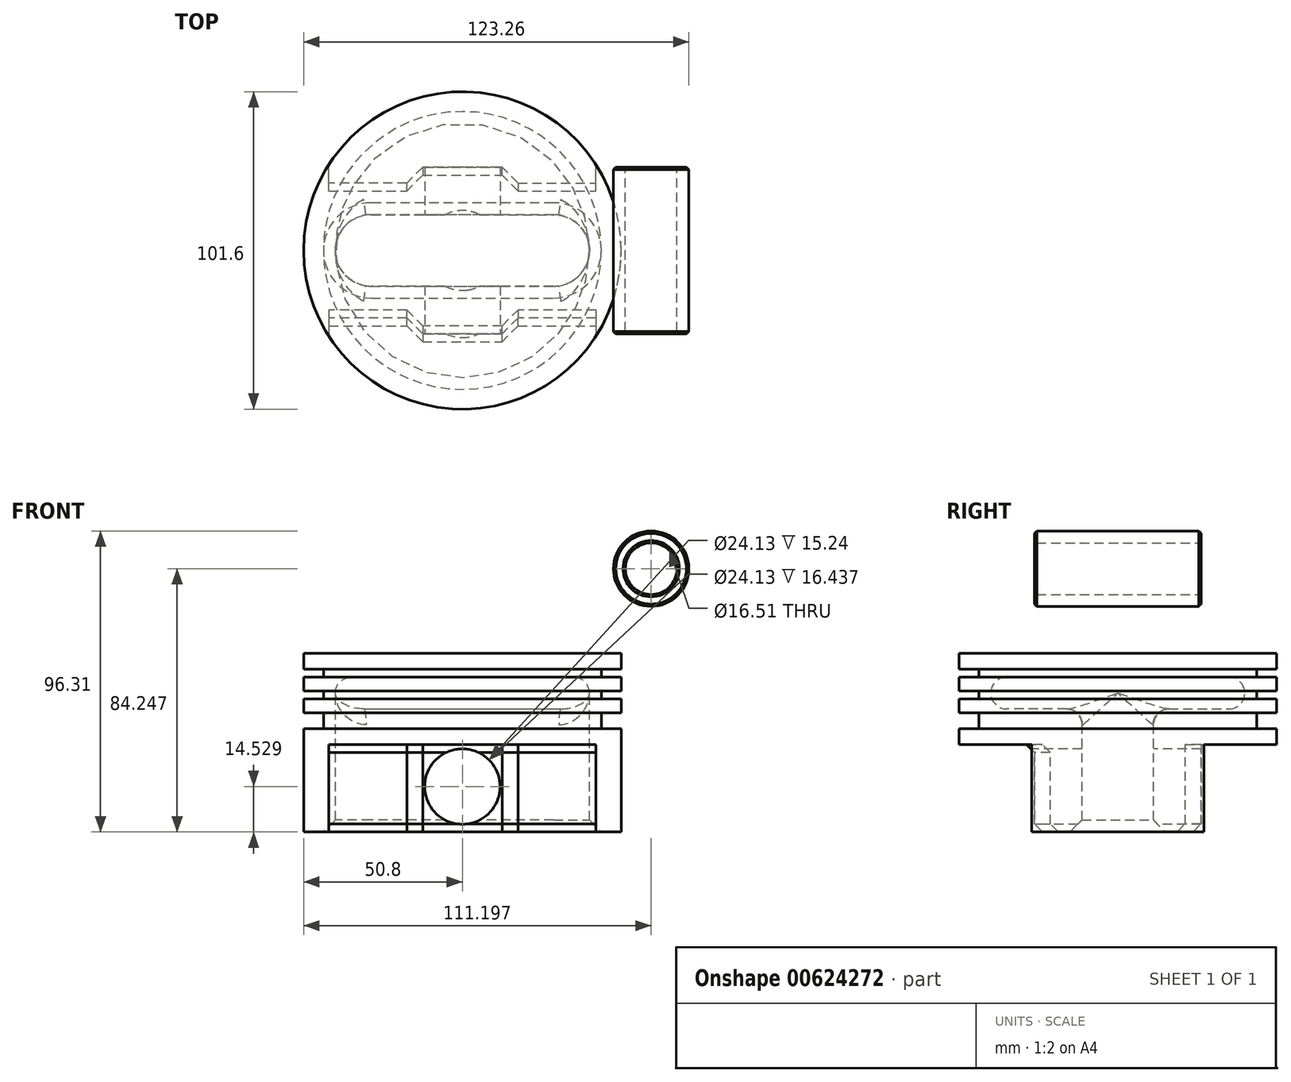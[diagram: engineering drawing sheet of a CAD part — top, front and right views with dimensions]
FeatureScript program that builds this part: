
annotation { "Feature Type Name" : "Feature", "Feature Type Description" : "" }
export const myFeature = defineFeature(function(context is Context, id is Id, definition is map)
    precondition{}
    {
        {
            var Q0;
            Q0=qCreatedBy(makeId("Front.planeOp"),FACE);
            var sketch = newSketch(context, id + "F0", { "sketchPlane" : qUnion([Q0])});
            skLineSegment(sketch, "E0", {"start": v(0, 42.2) * mm, "end": v(-50.8, 42.2) * mm});
            skLineSegment(sketch, "E1", {"start": v(-50.8, 42.2) * mm, "end": v(-50.8, 37.11) * mm});
            skLineSegment(sketch, "E2", {"start": v(-50.8, 37.11) * mm, "end": v(-44.45, 37.11) * mm});
            skLineSegment(sketch, "E3", {"start": v(-44.45, 37.11) * mm, "end": v(-44.45, 34.57) * mm});
            skLineSegment(sketch, "E4", {"start": v(-44.45, 34.57) * mm, "end": v(-50.8, 34.57) * mm});
            skLineSegment(sketch, "E5", {"start": v(-50.8, 34.57) * mm, "end": v(-50.8, 30.13) * mm});
            skLineSegment(sketch, "E6", {"start": v(-50.8, 30.13) * mm, "end": v(-44.45, 30.13) * mm});
            skLineSegment(sketch, "E7", {"start": v(-44.45, 30.13) * mm, "end": v(-44.45, 27.59) * mm});
            skLineSegment(sketch, "E8", {"start": v(-44.45, 27.59) * mm, "end": v(-50.8, 27.59) * mm});
            skLineSegment(sketch, "E9", {"start": v(-50.8, 27.59) * mm, "end": v(-50.8, 23.14) * mm});
            skLineSegment(sketch, "E10", {"start": v(-50.8, 23.14) * mm, "end": v(-44.45, 23.14) * mm});
            skLineSegment(sketch, "E11", {"start": v(-44.45, 23.14) * mm, "end": v(-44.45, 18.06) * mm});
            skLineSegment(sketch, "E12", {"start": v(-44.45, 18.06) * mm, "end": v(-50.8, 18.06) * mm});
            skLineSegment(sketch, "E13", {"start": v(-50.8, 18.06) * mm, "end": v(-50.8, 12.98) * mm});
            skLineSegment(sketch, "E14", {"start": v(-50.8, 12.98) * mm, "end": v(0, 12.98) * mm});
            skLineSegment(sketch, "E15", {"start": v(0, 34.57) * mm, "end": v(-35.56, 34.57) * mm});
            skLineSegment(sketch, "E16", {"start": v(0, 24.41) * mm, "end": v(-35.56, 24.41) * mm});
            skArc(sketch, "E17", {"start": v(-35.56, 34.57) * mm, "mid": v(-40.64, 29.5) * mm, "end": v(-35.56, 24.41) * mm});
            skLineSegment(sketch, "E18", {"start": v(0, 42.2) * mm, "end": v(0, 12.98) * mm});
            skSolve(sketch);
        }
        {
            var Q0;
            {var subQ0=sQuery(id+"F0.wireOp",EDGE,"E0");Q0=makeQuery(id+"F0.imprint","IMPRINT",FACE,{"disambiguationData":[TD([[makeQuery(id+"F0.imprint","IMPRINT",EDGE,{"derivedFrom":subQ0}),1.0]])]});}
            var Q1;
            Q1=sQuery(id+"F0.wireOp",EDGE,"E18");
            revolve(context, id + "F1", {"entities" : qUnion([Q0]), "axis" : qUnion([Q1]), "revolveType" : RevolveType.FULL});
        }
        {
            var Q0;
            Q0=makeQuery(id+"F1.opRevolve","SWEPT_FACE",FACE,{"disambiguationData":[OSD([sQuery(id+"F0.wireOp",EDGE,"E14")])]});
            var sketch = newSketch(context, id + "F2", { "sketchPlane" : qUnion([Q0])});
            skLineSegment(sketch, "E19", {"start": v(0, 11.43) * mm, "end": v(-29.21, 11.43) * mm});
            skLineSegment(sketch, "E20", {"start": v(-15.24, 21.6) * mm, "end": v(-42.7, 21.59) * mm});
            skLineSegment(sketch, "E21", {"start": v(-42.7, 21.59) * mm, "end": v(-42.7, 27.52) * mm});
            skLineSegment(sketch, "E22.MirrorCS", {"start": v(0, 11.43) * mm, "end": v(29.21, 11.43) * mm});
            skLineSegment(sketch, "E23.MirrorCS", {"start": v(15.24, 21.6) * mm, "end": v(42.7, 21.59) * mm});
            skLineSegment(sketch, "E24.MirrorCS", {"start": v(42.7, 21.59) * mm, "end": v(42.7, 27.52) * mm});
            skLineSegment(sketch, "E25.MirrorCS", {"start": v(0, -11.43) * mm, "end": v(-29.21, -11.43) * mm});
            skLineSegment(sketch, "E26.MirrorCS", {"start": v(0, -11.43) * mm, "end": v(29.21, -11.43) * mm});
            skLineSegment(sketch, "E27.MirrorCS", {"start": v(15.24, -21.6) * mm, "end": v(42.7, -21.59) * mm});
            skLineSegment(sketch, "E28.MirrorCS", {"start": v(-15.24, -21.6) * mm, "end": v(-42.7, -21.59) * mm});
            skLineSegment(sketch, "E29.MirrorCS", {"start": v(-42.7, -21.59) * mm, "end": v(-42.7, -27.52) * mm});
            skLineSegment(sketch, "E30.MirrorCS", {"start": v(42.7, -21.59) * mm, "end": v(42.7, -27.52) * mm});
            skArc(sketch, "E31", {"start": v(-29.21, 11.43) * mm, "mid": v(-40.64, 0) * mm, "end": v(-29.21, -11.43) * mm});
            skLineSegment(sketch, "E32", {"start": v(-15.24, 21.6) * mm, "end": v(-15.24, 26.67) * mm});
            skLineSegment(sketch, "E33", {"start": v(-15.24, 26.67) * mm, "end": v(0, 26.67) * mm});
            skLineSegment(sketch, "E34.MirrorCS", {"start": v(15.24, 26.67) * mm, "end": v(0, 26.67) * mm});
            skLineSegment(sketch, "E35.MirrorCS", {"start": v(15.24, 21.6) * mm, "end": v(15.24, 26.67) * mm});
            skLineSegment(sketch, "E36.MirrorCS", {"start": v(15.24, -26.67) * mm, "end": v(0, -26.67) * mm});
            skLineSegment(sketch, "E37.MirrorCS", {"start": v(-15.24, -26.67) * mm, "end": v(0, -26.67) * mm});
            skLineSegment(sketch, "E38.MirrorCS", {"start": v(-15.24, -21.6) * mm, "end": v(-15.24, -26.67) * mm});
            skLineSegment(sketch, "E39.MirrorCS", {"start": v(15.24, -21.6) * mm, "end": v(15.24, -26.67) * mm});
            skPoint(sketch, "E40.orphan", {"position": v(0, 21.6) * mm});
            skPoint(sketch, "E41.orphan", {"position": v(0, -21.6) * mm});
            skArc(sketch, "E42", {"start": v(29.21, 11.43) * mm, "mid": v(40.64, 0) * mm, "end": v(29.21, -11.43) * mm});
            skSolve(sketch);
        }
        {
            var Q0;
            Q0=makeQuery(id+"F2.imprint","IMPRINT",FACE,{"disambiguationData":[TD([[makeQuery(id+"F2.imprint","IMPRINT",EDGE,{"derivedFrom":sQuery(id+"F2.wireOp",EDGE,"E19")}),-1.0]])]});
            extrude(context, id + "F3", {"entities" : qUnion([Q0]), "operationType" : NewBodyOperationType.ADD, "depth" : 27.94 * mm, "offsetDistance" : 25.4 * mm});
        }
        {
            var Q0;
            Q0=makeQuery(id+"F3.opExtrude","SWEPT_FACE",FACE,{"disambiguationData":[OSD([sQuery(id+"F2.wireOp",EDGE,"E33"),sQuery(id+"F2.wireOp",EDGE,"E34.MirrorCS")])]});
            var sketch = newSketch(context, id + "F4", { "sketchPlane" : qUnion([Q0])});
            skCircle(sketch, "E43", {"center": v(0, -0.43) * mm, "radius": 12.07 * mm});
            skSolve(sketch);
        }
        {
            var Q0;
            Q0=makeQuery(id+"F3.boolean.opBoolean","SPLIT",FACE,{"disambiguationData":[TD([makeQuery(id+"F3.opExtrude","SWEPT_FACE",FACE,{"disambiguationData":[OSD([sQuery(id+"F2.wireOp",EDGE,"E31")])]})])],"derivedFrom":makeQuery(id+"F1.opRevolve","SWEPT_FACE",FACE,{"disambiguationData":[OSD([sQuery(id+"F0.wireOp",EDGE,"E14")])]})});
            extrude(context, id + "F5", {"entities" : qUnion([Q0]), "operationType" : NewBodyOperationType.REMOVE, "oppositeDirection" : true, "depth" : 16.5 * mm, "offsetDistance" : 25.4 * mm});
        }
        {
            var Q0;
            Q0=makeQuery(id+"F5.boolean.opBoolean","INTERSECT",EDGE,{"disambiguationData":[OD(1.0)],"derivedFrom":[makeQuery(id+"F1.opRevolve","SWEPT_FACE",FACE,{"disambiguationData":[OSD([sQuery(id+"F0.wireOp",EDGE,"E17")])]}),makeQuery(id+"F5.opExtrude","SWEPT_FACE",FACE,{"disambiguationData":[OSD([sQuery(id+"F2.wireOp",EDGE,"E42")])]})]});
            var Q1;
            Q1=makeQuery(id+"F5.boolean.opBoolean","INTERSECT",EDGE,{"disambiguationData":[OD(0.0)],"derivedFrom":[makeQuery(id+"F1.opRevolve","SWEPT_FACE",FACE,{"disambiguationData":[OSD([sQuery(id+"F0.wireOp",EDGE,"E16")])]}),makeQuery(id+"F5.opExtrude","SWEPT_FACE",FACE,{"disambiguationData":[OSD([sQuery(id+"F2.wireOp",EDGE,"E42")])]})]});
            var Q2;
            Q2=makeQuery(id+"F5.boolean.opBoolean","INTERSECT",EDGE,{"derivedFrom":[makeQuery(id+"F1.opRevolve","SWEPT_FACE",FACE,{"disambiguationData":[OSD([sQuery(id+"F0.wireOp",EDGE,"E16")])]}),makeQuery(id+"F5.opExtrude","SWEPT_FACE",FACE,{"disambiguationData":[OSD([sQuery(id+"F2.wireOp",EDGE,"E19"),sQuery(id+"F2.wireOp",EDGE,"E22.MirrorCS")])]})]});
            fillet(context, id + "F6", {"entities" : qUnion([Q0, Q1, Q2]), "radius" : 5.08 * mm, "tangentPropagation" : true, "allowEdgeOverflow" : false});
        }
        {
            var Q0;
            Q0 = qSketchRegion(id + "F4", true);
            extrude(context, id + "F7", {"entities" : qUnion([Q0]), "operationType" : NewBodyOperationType.REMOVE, "endBound" : BoundingType.SYMMETRIC, "oppositeDirection" : true, "depth" : 223 * mm, "offsetDistance" : 25.4 * mm});
        }
        {
            var Q0;
            Q0=makeQuery(id+"F3.opExtrude","CAP_EDGE",EDGE,{"disambiguationData":[OSD([sQuery(id+"F2.wireOp",EDGE,"E31")])],"isStart":false});
            chamfer(context, id + "F8", {"entities" : qUnion([Q0]), "width" : 3.8 * mm, "tangentPropagation" : true});
        }
        {
            var Q0;
            Q0=makeQuery(id+"F3.opExtrude","SWEPT_EDGE",EDGE,{"disambiguationData":[OSD([sQuery(id+"F2.wireOp",EDGE,"E27.MirrorCS"),sQuery(id+"F2.wireOp",EDGE,"E39.MirrorCS")])]});
            var Q1;
            Q1=makeQuery(id+"F3.opExtrude","SWEPT_EDGE",EDGE,{"disambiguationData":[OSD([sQuery(id+"F2.wireOp",EDGE,"E36.MirrorCS"),sQuery(id+"F2.wireOp",EDGE,"E39.MirrorCS")])]});
            var Q2;
            Q2=makeQuery(id+"F3.opExtrude","CAP_EDGE",EDGE,{"disambiguationData":[OSD([sQuery(id+"F2.wireOp",EDGE,"E36.MirrorCS"),sQuery(id+"F2.wireOp",EDGE,"E37.MirrorCS")])],"isStart":false});
            var Q3;
            Q3=makeQuery(id+"F3.opExtrude","CAP_EDGE",EDGE,{"disambiguationData":[OSD([sQuery(id+"F2.wireOp",EDGE,"E39.MirrorCS")])],"isStart":false});
            var Q4;
            Q4=makeQuery(id+"F3.opExtrude","CAP_EDGE",EDGE,{"disambiguationData":[OSD([sQuery(id+"F2.wireOp",EDGE,"E38.MirrorCS")])],"isStart":false});
            var Q5;
            Q5=makeQuery(id+"F3.opExtrude","SWEPT_EDGE",EDGE,{"disambiguationData":[OSD([sQuery(id+"F2.wireOp",EDGE,"E28.MirrorCS"),sQuery(id+"F2.wireOp",EDGE,"E38.MirrorCS")])]});
            var Q6;
            Q6=makeQuery(id+"F3.opExtrude","SWEPT_EDGE",EDGE,{"disambiguationData":[OSD([sQuery(id+"F2.wireOp",EDGE,"E37.MirrorCS"),sQuery(id+"F2.wireOp",EDGE,"E38.MirrorCS")])]});
            var Q7;
            Q7=makeQuery(id+"F3.opExtrude","CAP_EDGE",EDGE,{"disambiguationData":[OSD([sQuery(id+"F2.wireOp",EDGE,"E28.MirrorCS")])],"isStart":true});
            var Q8;
            Q8=makeQuery(id+"F3.opExtrude","CAP_EDGE",EDGE,{"disambiguationData":[OSD([sQuery(id+"F2.wireOp",EDGE,"E27.MirrorCS")])],"isStart":true});
            var Q9;
            Q9=makeQuery(id+"F3.opExtrude","CAP_EDGE",EDGE,{"disambiguationData":[OSD([sQuery(id+"F2.wireOp",EDGE,"E38.MirrorCS")])],"isStart":true});
            var Q10;
            Q10=makeQuery(id+"F3.opExtrude","CAP_EDGE",EDGE,{"disambiguationData":[OSD([sQuery(id+"F2.wireOp",EDGE,"E20")])],"isStart":true});
            var Q11;
            Q11=makeQuery(id+"F3.opExtrude","SWEPT_EDGE",EDGE,{"disambiguationData":[OSD([sQuery(id+"F2.wireOp",EDGE,"E20"),sQuery(id+"F2.wireOp",EDGE,"E32")])]});
            var Q12;
            Q12=makeQuery(id+"F3.opExtrude","SWEPT_EDGE",EDGE,{"disambiguationData":[OSD([sQuery(id+"F2.wireOp",EDGE,"E34.MirrorCS"),sQuery(id+"F2.wireOp",EDGE,"E35.MirrorCS")])]});
            var Q13;
            Q13=makeQuery(id+"F3.opExtrude","CAP_EDGE",EDGE,{"disambiguationData":[OSD([sQuery(id+"F2.wireOp",EDGE,"E32")])],"isStart":true});
            var Q14;
            Q14=makeQuery(id+"F3.opExtrude","SWEPT_EDGE",EDGE,{"disambiguationData":[OSD([sQuery(id+"F2.wireOp",EDGE,"E32"),sQuery(id+"F2.wireOp",EDGE,"E33")])]});
            var Q15;
            Q15=makeQuery(id+"F3.opExtrude","CAP_EDGE",EDGE,{"disambiguationData":[OSD([sQuery(id+"F2.wireOp",EDGE,"E23.MirrorCS")])],"isStart":false});
            var Q16;
            Q16=makeQuery(id+"F3.opExtrude","CAP_EDGE",EDGE,{"disambiguationData":[OSD([sQuery(id+"F2.wireOp",EDGE,"E23.MirrorCS")])],"isStart":true});
            var Q17;
            Q17=makeQuery(id+"F3.opExtrude","CAP_EDGE",EDGE,{"disambiguationData":[OSD([sQuery(id+"F2.wireOp",EDGE,"E35.MirrorCS")])],"isStart":false});
            var Q18;
            Q18=makeQuery(id+"F3.opExtrude","CAP_EDGE",EDGE,{"disambiguationData":[OSD([sQuery(id+"F2.wireOp",EDGE,"E32")])],"isStart":false});
            var Q19;
            Q19=makeQuery(id+"F3.opExtrude","CAP_EDGE",EDGE,{"disambiguationData":[OSD([sQuery(id+"F2.wireOp",EDGE,"E20")])],"isStart":false});
            var Q20;
            Q20=makeQuery(id+"F3.opExtrude","SWEPT_EDGE",EDGE,{"disambiguationData":[OSD([sQuery(id+"F2.wireOp",EDGE,"E23.MirrorCS"),sQuery(id+"F2.wireOp",EDGE,"E35.MirrorCS")])]});
            var Q21;
            Q21=makeQuery(id+"F3.opExtrude","CAP_EDGE",EDGE,{"disambiguationData":[OSD([sQuery(id+"F2.wireOp",EDGE,"E33"),sQuery(id+"F2.wireOp",EDGE,"E34.MirrorCS")])],"isStart":false});
            chamfer(context, id + "F9", {"entities" : qUnion([Q0, Q1, Q2, Q3, Q4, Q5, Q6, Q7, Q8, Q9, Q10, Q11, Q12, Q13, Q14, Q15, Q16, Q17, Q18, Q19, Q20, Q21]), "width" : 2.54 * mm, "tangentPropagation" : true});
        }
        {
            var Q0;
            Q0=qCreatedBy(makeId("Front.planeOp"),FACE);
            var sketch = newSketch(context, id + "F10", { "sketchPlane" : qUnion([Q0])});
            skCircle(sketch, "E44", {"center": v(60.4, 69.29) * mm, "radius": 12.07 * mm});
            skCircle(sketch, "E45.0", {"center": v(60.4, 69.29) * mm, "radius": 8.26 * mm});
            skSolve(sketch);
        }
        {
            var Q0;
            Q0=makeQuery(id+"F10.imprint","IMPRINT",FACE,{"disambiguationData":[TD([[makeQuery(id+"F10.imprint","IMPRINT",EDGE,{"derivedFrom":sQuery(id+"F10.wireOp",EDGE,"E44")}),1.0]])]});
            extrude(context, id + "F11", {"entities" : qUnion([Q0]), "endBound" : BoundingType.SYMMETRIC, "depth" : 53.34 * mm, "offsetDistance" : 25.4 * mm});
        }
        {
            var Q0;
            Q0=makeQuery(id+"F11.opExtrude","CAP_EDGE",EDGE,{"disambiguationData":[OSD([sQuery(id+"F10.wireOp",EDGE,"E45.0")])],"isStart":true});
            var Q1;
            Q1=makeQuery(id+"F11.opExtrude","CAP_EDGE",EDGE,{"disambiguationData":[OSD([sQuery(id+"F10.wireOp",EDGE,"E44")])],"isStart":true});
            var Q2;
            Q2=makeQuery(id+"F11.opExtrude","CAP_FACE",FACE,{"disambiguationData":[OSD([sQuery(id+"F10.wireOp",EDGE,"E44"),sQuery(id+"F10.wireOp",EDGE,"E45.0")])],"isStart":false});
            chamfer(context, id + "F12", {"entities" : qUnion([Q0, Q1, Q2]), "width" : 0.76 * mm, "tangentPropagation" : true});
        }
    });
